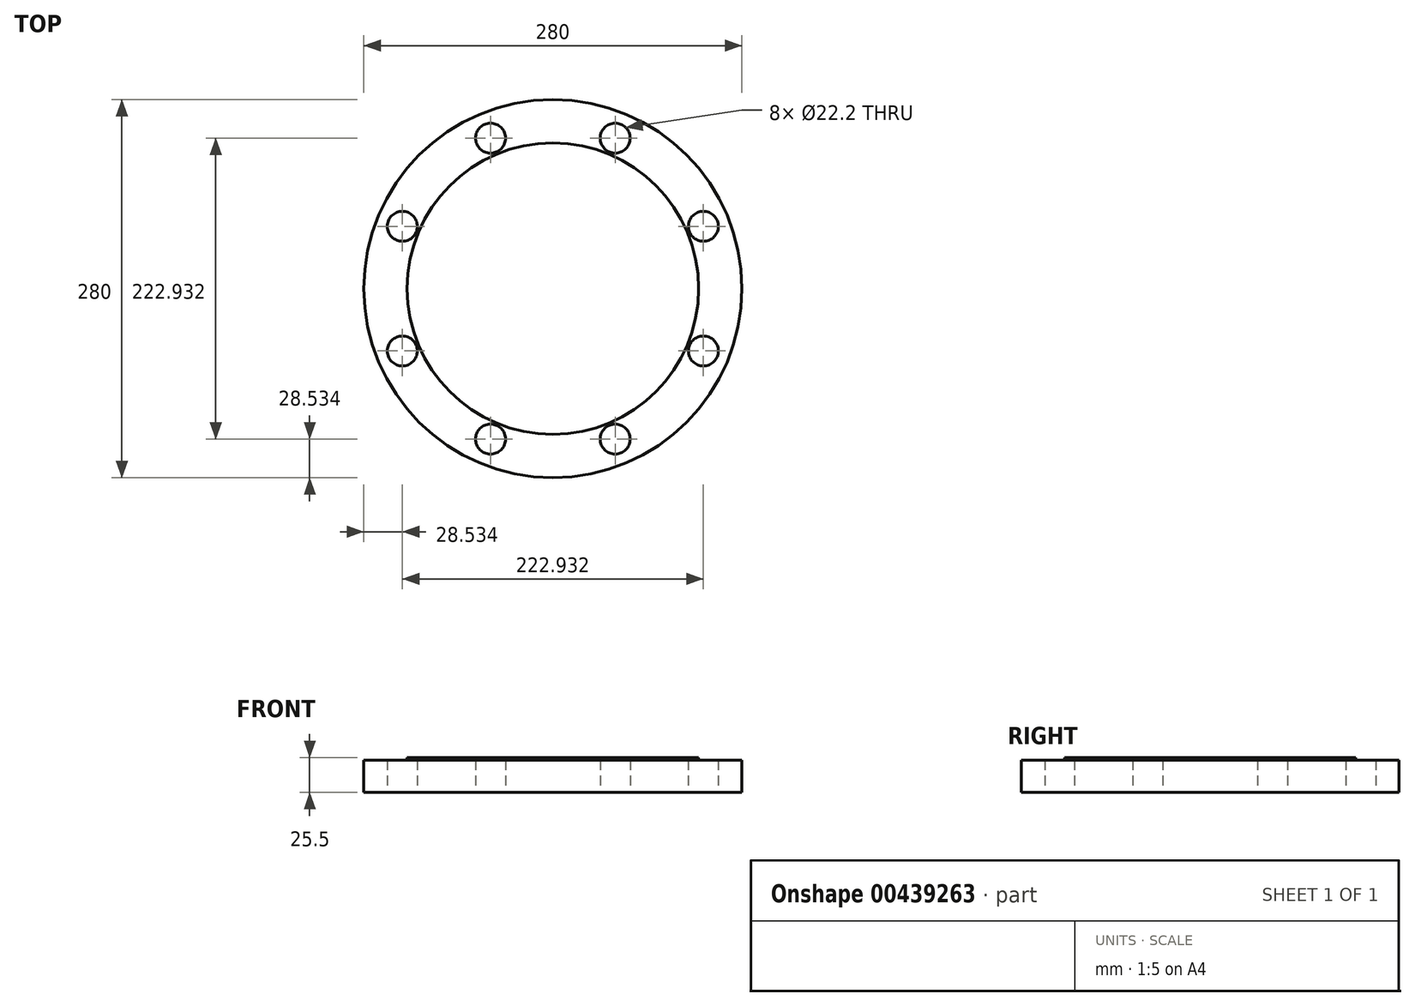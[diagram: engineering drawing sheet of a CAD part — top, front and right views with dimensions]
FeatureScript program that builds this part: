
annotation { "Feature Type Name" : "Feature", "Feature Type Description" : "" }
export const myFeature = defineFeature(function(context is Context, id is Id, definition is map)
    precondition{}
    {
        {
            assignVariable(context, id + "F0", {"name" : "B_THK", "anyValue" : 23.9});
        }
        {
            assignVariable(context, id + "F1", {"name" : "B_with_RF", "anyValue" : 25.5});
        }
        {
            var Q0;
            Q0=qCreatedBy(makeId("Top.planeOp"),FACE);
            var sketch = newSketch(context, id + "F2", { "sketchPlane" : qUnion([Q0])});
            skCircle(sketch, "E0", {"center": v(0, 0) * mm, "radius": 120.65 * mm, "construction": true});
            skCircle(sketch, "E1", {"center": v(0, 0) * mm, "radius": 107.95 * mm});
            skCircle(sketch, "E2", {"center": v(0, 0) * mm, "radius": 140 * mm});
            skLineSegment(sketch, "E3", {"start": v(0, 0) * mm, "end": v(0, -170) * mm, "construction": true});
            skLineSegment(sketch, "E4", {"start": v(0, 0) * mm, "end": v(46.17, -111.47) * mm, "construction": true});
            skCircle(sketch, "E5", {"center": v(46.17, -111.47) * mm, "radius": 11.1 * mm});
            skCircle(sketch, "E6.1.0", {"center": v(111.47, -46.17) * mm, "radius": 11.1 * mm});
            skCircle(sketch, "E6.2.0", {"center": v(111.47, 46.17) * mm, "radius": 11.1 * mm});
            skCircle(sketch, "E6.3.0", {"center": v(46.17, 111.47) * mm, "radius": 11.1 * mm});
            skCircle(sketch, "E7.1.4.0", {"center": v(-46.17, 111.47) * mm, "radius": 11.1 * mm});
            skCircle(sketch, "E7.1.5.0", {"center": v(-111.47, 46.17) * mm, "radius": 11.1 * mm});
            skCircle(sketch, "E7.1.6.0", {"center": v(-111.47, -46.17) * mm, "radius": 11.1 * mm});
            skCircle(sketch, "E7.1.7.0", {"center": v(-46.17, -111.47) * mm, "radius": 11.1 * mm});
            skSolve(sketch);
        }
        {
            var Q0;
            Q0=makeQuery(id+"F2.imprint","IMPRINT",FACE,{"disambiguationData":[TD([[makeQuery(id+"F2.imprint","IMPRINT",EDGE,{"derivedFrom":sQuery(id+"F2.wireOp",EDGE,"E1")}),1.0]])]});
            var sketch = newSketch(context, id + "F3", { "sketchPlane" : qUnion([Q0])});
            skLineSegment(sketch, "E8", {"start": v(-70, -80.86) * mm, "end": v(-70, -220.47) * mm});
            skLineSegment(sketch, "E9", {"start": v(70, -220.47) * mm, "end": v(70, -80.86) * mm});
            skLineSegment(sketch, "E10", {"start": v(-70, -220.47) * mm, "end": v(70, -220.47) * mm});
            skLineSegment(sketch, "E11", {"start": v(-70, -80.86) * mm, "end": v(70, -80.86) * mm, "construction": true});
            skCircle(sketch, "E12", {"center": v(0, 0) * mm, "radius": 106.95 * mm});
            skLineSegment(sketch, "E13.bottom", {"start": v(-75, -220.47) * mm, "end": v(75, -220.47) * mm});
            skLineSegment(sketch, "E13.top", {"start": v(-75, -230.47) * mm, "end": v(75, -230.47) * mm});
            skLineSegment(sketch, "E13.left", {"start": v(-75, -220.47) * mm, "end": v(-75, -230.47) * mm});
            skLineSegment(sketch, "E13.right", {"start": v(75, -220.47) * mm, "end": v(75, -230.47) * mm});
            skPoint(sketch, "E14", {"position": v(0, -230.47) * mm});
            skSolve(sketch);
        }
        {
            var Q0;
            Q0=makeQuery(id+"F2.imprint","IMPRINT",FACE,{"disambiguationData":[TD([[makeQuery(id+"F2.imprint","IMPRINT",EDGE,{"derivedFrom":sQuery(id+"F2.wireOp",EDGE,"E1")}),-1.0]])]});
            var Q1;
            Q1=makeQuery(id+"F2.imprint","IMPRINT",FACE,{"disambiguationData":[TD([[makeQuery(id+"F2.imprint","IMPRINT",EDGE,{"derivedFrom":sQuery(id+"F2.wireOp",EDGE,"E1")}),1.0]])]});
            extrude(context, id + "F4", {"entities" : qUnion([Q0, Q1]), "depth" : (getVariable(context, 'B_THK')) * mm, "offsetDistance" : 25 * mm});
        }
        {
            var Q0;
            {var subQ0=sQuery(id+"F3.wireOp",EDGE,"nsYsx9z4-e8ki-qo67-oDX8-4oPPJJXHgKWi");Q0=makeQuery(id+"F3.imprint","IMPRINT",FACE,{"disambiguationData":[TD([[makeQuery(id+"F3.imprint","IMPRINT",EDGE,{"derivedFrom":subQ0}),1.0]])]});}
            var Q1;
            Q1=makeQuery(id+"F2.imprint","IMPRINT",FACE,{"disambiguationData":[TD([[makeQuery(id+"F2.imprint","IMPRINT",EDGE,{"derivedFrom":sQuery(id+"F2.wireOp",EDGE,"E1")}),1.0]])]});
            extrude(context, id + "F5", {"entities" : qUnion([Q0, Q1]), "operationType" : NewBodyOperationType.ADD, "depth" : (getVariable(context, 'B_with_RF')) * mm, "offsetDistance" : 25 * mm});
        }
    });
